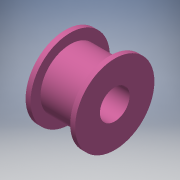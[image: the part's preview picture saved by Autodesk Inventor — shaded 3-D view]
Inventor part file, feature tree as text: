
AUTODESK INVENTOR PART (.ipt)
format: ipt  version: 2017 SP1 (Build 210196100, 196)  size: 142,336 bytes
history: native  units: in
note: dims shown in document units (in); Inventor stores cm internally (conversion verified against a paired STEP export)
features: extrude x4, sketch x4
ambient origin geometry x8: Origin, YZ Plane, XZ Plane, XY Plane, X Axis, Y Axis, Z Axis, Center Point
bodies: Solid1 (feature_tree)
feature tree (8):
  extrude  "Extrusion1"  Depth=0.375in
  extrude  "Extrusion2"  Depth=0.5in
  extrude  "Extrusion3"  Depth=0.0625in TaperAngle=0.0deg
  extrude  "Extrusion4"  Depth=0.1875in TaperAngle=0.0deg
  sketch  "Sketch1"  dims[d0=1.125in d2=0.375in]
  sketch  "Sketch2"  dims[d4=0.5in d5=0.0in d6=0.125in]
  sketch  "Sketch3"  dims[d7=0.0625in d8=0.0in d9=0.0625in d10=0.0in]
  sketch  "Sketch4"  dims[d11=0.1875in d12=0.375in d13=0.0in]
